# Revit family: Haworth_Enclose_Accessories_WallEnd
name_source: partatom
category: Furniture Systems
revit_build: Autodesk Revit 2018 (Build: 20170223_1515(x64)
units: mm (PartAtom-declared; Revit-internal decimal feet)

## family parameters
Always vertical = Yes
Cut with Voids When Loaded = No
OmniClass Number = 23.25.40.14
OmniClass Title = Demountable Partitions
Part Type = Normal
Room Calculation Point = No
Round Connector Dimension = Use Diameter
Shared = No
Work Plane-Based = No

## types (4) — shared parameters
Actual Height = 108 "
Assembly Code = C1010200
Depth = 4 "
Description = Haworth - Enclose Accessories Wall - End
Frame Finish = Haworth _ Metal _ Brushed Aluminum
Height = 108 "
Manufacturer = Haworth
Material Options = http://surfaces.haworth.com
Max. Height = 144 "
Min. Height = 84 "
Min/Max Height = 84-144 in.
Model = Haworth_Enclose-Accessories-Wall_End
Revision Number = 3
Sustainability Info = http://www.haworth.com
URL = www.haworth.com
URL - Product = http://www.haworth.com
Warranty = http://www.haworth.com

## per-type parameters (varying)
| type | End of Run Module | Width |
| Centerline Module | No | 1.845 " |
| 3 Way_Centerline Module_Intersection_90 | No | 0.155 " |
| Low Profile | Yes | 0.875 " |
| Systems Module | Yes | 3.845 " |

type visibility flags (boolean, named after types; folded from table):
- Centerline Module: Yes: Centerline Module Intersection
- 3 Way_Centerline Module_Intersection_90: Yes: Centerline Module Intersection
- Low Profile: Yes: (none)
- Systems Module: Yes: (none)

## geometry (parser evidence)
native form markers: Sweep x3
no freeform markers — native parametric forms only
